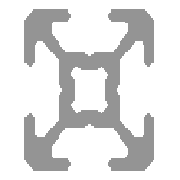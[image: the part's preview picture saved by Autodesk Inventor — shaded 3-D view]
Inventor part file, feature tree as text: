
AUTODESK INVENTOR PART (.ipt)
format: ipt  version: 2016 (Build 200138000, 138)  size: 380,928 bytes
history: native  units: mm
features: other x7, extrude x1, sketch x1
ambient origin geometry x8: Origin, YZ Plane, XZ Plane, XY Plane, X Axis, Y Axis, Z Axis, Center Point
bodies: Body1 (feature_tree)
feature tree (9):
  other  "20x20"
  other  "Table"
  other  "20x20-30"
  other  "20x20-360"
  other  "20x20-750"
  other  "Blocks"
  extrude  "Extrusion3"  [1 undecoded]
  sketch  "Sketch1"  dims[d23=0.0mm]
  other  "20x20:1"
note: 1 required parameter value undecoded (feature->parameter linkage not recoverable at this tier; creation-order binding heuristic only, values carry confidence <= 0.55)
